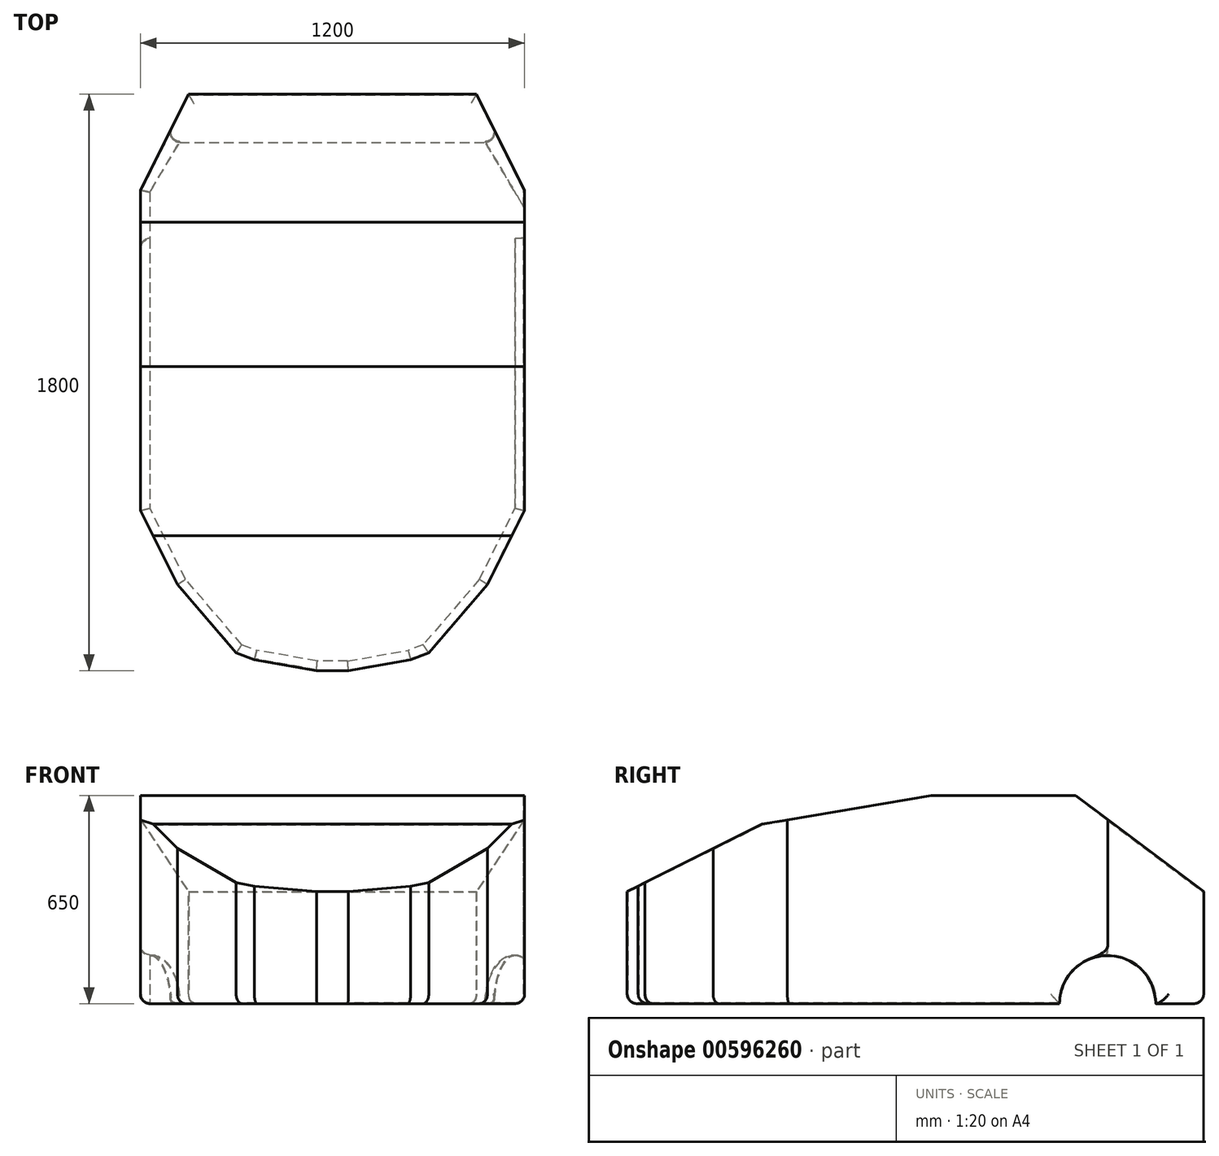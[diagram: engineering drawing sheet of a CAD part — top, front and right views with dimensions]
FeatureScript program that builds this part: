
annotation { "Feature Type Name" : "Feature", "Feature Type Description" : "" }
export const myFeature = defineFeature(function(context is Context, id is Id, definition is map)
    precondition{}
    {
        {
            var Q0;
            Q0=qCreatedBy(makeId("Top.planeOp"),FACE);
            var sketch = newSketch(context, id + "F0", { "sketchPlane" : qUnion([Q0])});
            skLineSegment(sketch, "E0.bottom", {"start": v(600, 900) * mm, "end": v(-600, 900) * mm});
            skLineSegment(sketch, "E0.top", {"start": v(600, -900) * mm, "end": v(-600, -900) * mm});
            skLineSegment(sketch, "E0.left", {"start": v(600, 900) * mm, "end": v(600, -900) * mm});
            skLineSegment(sketch, "E0.right", {"start": v(-600, 900) * mm, "end": v(-600, -900) * mm});
            skPoint(sketch, "E0.middle", {"position": v(0, 0) * mm});
            skSolve(sketch);
        }
        {
            var Q0;
            Q0=makeQuery(id+"F0.imprint","IMPRINT",FACE,{"disambiguationData":[TD([[makeQuery(id+"F0.imprint","IMPRINT",EDGE,{"derivedFrom":sQuery(id+"F0.wireOp",EDGE,"E0.bottom")}),1.0]])]});
            extrude(context, id + "F1", {"entities" : qUnion([Q0]), "depth" : 650 * mm, "offsetDistance" : 25 * mm});
        }
        {
            var Q0;
            Q0=makeQuery(id+"F1.opExtrude","CAP_EDGE",EDGE,{"disambiguationData":[OSD([sQuery(id+"F0.wireOp",EDGE,"E0.top")])],"isStart":false});
            chamfer(context, id + "F2", {"entities" : qUnion([Q0]), "chamferType" : ChamferType.TWO_OFFSETS, "width1" : 300 * mm, "oppositeDirection" : false, "width2" : 600 * mm, "tangentPropagation" : true});
        }
        {
            var Q0;
            Q0=makeQuery(id+"F1.opExtrude","CAP_EDGE",EDGE,{"disambiguationData":[OSD([sQuery(id+"F0.wireOp",EDGE,"E0.bottom")])],"isStart":false});
            chamfer(context, id + "F3", {"entities" : qUnion([Q0]), "chamferType" : ChamferType.TWO_OFFSETS, "width1" : 400 * mm, "oppositeDirection" : false, "width2" : 300 * mm, "tangentPropagation" : true});
        }
        {
            var Q0;
            Q0=makeQuery(id+"F1.opExtrude","SWEPT_EDGE",EDGE,{"disambiguationData":[OSD([sQuery(id+"F0.wireOp",EDGE,"E0.top"),sQuery(id+"F0.wireOp",EDGE,"E0.left")])]});
            var Q1;
            Q1=makeQuery(id+"F1.opExtrude","SWEPT_EDGE",EDGE,{"disambiguationData":[OSD([sQuery(id+"F0.wireOp",EDGE,"E0.top"),sQuery(id+"F0.wireOp",EDGE,"E0.right")])]});
            chamfer(context, id + "F4", {"entities" : qUnion([Q0, Q1]), "chamferType" : ChamferType.TWO_OFFSETS, "width1" : 500 * mm, "oppositeDirection" : false, "width2" : 250 * mm, "tangentPropagation" : true});
        }
        {
            var Q0;
            {var subQ0=sQuery(id+"F0.wireOp",EDGE,"E0.top");Q0=makeQuery(id+"F4.opChamfer","BLEND_EDGE",EDGE,{"blendedFrom":[makeQuery(id+"F1.opExtrude","SWEPT_EDGE",EDGE,{"disambiguationData":[OSD([subQ0,sQuery(id+"F0.wireOp",EDGE,"E0.left")])]}),makeQuery(id+"F1.opExtrude","SWEPT_FACE",FACE,{"disambiguationData":[OSD([subQ0])]})],"blendedInto":[makeQuery(id+"F1.opExtrude","SWEPT_FACE",FACE,{"disambiguationData":[OSD([subQ0])]})]});}
            var Q1;
            {var subQ0=sQuery(id+"F0.wireOp",EDGE,"E0.top");Q1=makeQuery(id+"F4.opChamfer","BLEND_EDGE",EDGE,{"blendedFrom":[makeQuery(id+"F1.opExtrude","SWEPT_EDGE",EDGE,{"disambiguationData":[OSD([subQ0,sQuery(id+"F0.wireOp",EDGE,"E0.right")])]}),makeQuery(id+"F1.opExtrude","SWEPT_FACE",FACE,{"disambiguationData":[OSD([subQ0])]})],"blendedInto":[makeQuery(id+"F1.opExtrude","SWEPT_FACE",FACE,{"disambiguationData":[OSD([subQ0])]})]});}
            chamfer(context, id + "F5", {"entities" : qUnion([Q0, Q1]), "chamferType" : ChamferType.TWO_OFFSETS, "width1" : 200 * mm, "oppositeDirection" : false, "width2" : 100 * mm, "tangentPropagation" : true});
        }
        {
            var Q0;
            {var subQ0=sQuery(id+"F0.wireOp",EDGE,"E0.top");var subQ1=makeQuery(id+"F1.opExtrude","SWEPT_FACE",FACE,{"disambiguationData":[OSD([subQ0])]});Q0=makeQuery(id+"F5.opChamfer","BLEND_EDGE",EDGE,{"blendedFrom":[makeQuery(id+"F4.opChamfer","BLEND_EDGE",EDGE,{"blendedFrom":[makeQuery(id+"F1.opExtrude","SWEPT_EDGE",EDGE,{"disambiguationData":[OSD([subQ0,sQuery(id+"F0.wireOp",EDGE,"E0.right")])]}),subQ1],"blendedInto":[subQ1]}),subQ1],"blendedInto":[subQ1]});}
            var Q1;
            {var subQ0=sQuery(id+"F0.wireOp",EDGE,"E0.top");var subQ1=makeQuery(id+"F1.opExtrude","SWEPT_FACE",FACE,{"disambiguationData":[OSD([subQ0])]});Q1=makeQuery(id+"F5.opChamfer","BLEND_EDGE",EDGE,{"blendedFrom":[makeQuery(id+"F4.opChamfer","BLEND_EDGE",EDGE,{"blendedFrom":[makeQuery(id+"F1.opExtrude","SWEPT_EDGE",EDGE,{"disambiguationData":[OSD([subQ0,sQuery(id+"F0.wireOp",EDGE,"E0.left")])]}),subQ1],"blendedInto":[subQ1]}),subQ1],"blendedInto":[subQ1]});}
            chamfer(context, id + "F6", {"entities" : qUnion([Q0, Q1]), "chamferType" : ChamferType.TWO_OFFSETS, "width1" : 100 * mm, "oppositeDirection" : false, "width2" : 100 * mm, "tangentPropagation" : true});
        }
        {
            var Q0;
            {var subQ0=sQuery(id+"F0.wireOp",EDGE,"E0.top");Q0=makeQuery(id+"F2.opChamfer","BLEND_EDGE",EDGE,{"blendedFrom":[makeQuery(id+"F1.opExtrude","CAP_EDGE",EDGE,{"disambiguationData":[OSD([subQ0])],"isStart":false}),makeQuery(id+"F1.opExtrude","CAP_FACE",FACE,{"disambiguationData":[OSD([sQuery(id+"F0.wireOp",EDGE,"E0.bottom"),subQ0,sQuery(id+"F0.wireOp",EDGE,"E0.left"),sQuery(id+"F0.wireOp",EDGE,"E0.right")])],"isStart":false})],"blendedInto":[makeQuery(id+"F1.opExtrude","CAP_FACE",FACE,{"disambiguationData":[OSD([sQuery(id+"F0.wireOp",EDGE,"E0.bottom"),subQ0,sQuery(id+"F0.wireOp",EDGE,"E0.left"),sQuery(id+"F0.wireOp",EDGE,"E0.right")])],"isStart":false})]});}
            chamfer(context, id + "F7", {"entities" : qUnion([Q0]), "chamferType" : ChamferType.TWO_OFFSETS, "width1" : 350 * mm, "oppositeDirection" : false, "width2" : 200 * mm, "tangentPropagation" : true});
        }
        {
            var Q0;
            Q0=makeQuery(id+"F1.opExtrude","SWEPT_EDGE",EDGE,{"disambiguationData":[OSD([sQuery(id+"F0.wireOp",EDGE,"E0.bottom"),sQuery(id+"F0.wireOp",EDGE,"E0.left")])]});
            var Q1;
            Q1=makeQuery(id+"F1.opExtrude","SWEPT_EDGE",EDGE,{"disambiguationData":[OSD([sQuery(id+"F0.wireOp",EDGE,"E0.bottom"),sQuery(id+"F0.wireOp",EDGE,"E0.right")])]});
            chamfer(context, id + "F8", {"entities" : qUnion([Q0, Q1]), "chamferType" : ChamferType.TWO_OFFSETS, "width1" : 150 * mm, "oppositeDirection" : false, "width2" : 300 * mm, "tangentPropagation" : true});
        }
        {
            var Q0;
            {var subQ0=sQuery(id+"F0.wireOp",EDGE,"E0.left");var subQ1=sQuery(id+"F0.wireOp",EDGE,"E0.top");Q0=makeQuery(id+"F5.opChamfer","BLEND_EDGE",EDGE,{"blendedFrom":[makeQuery(id+"F4.opChamfer","BLEND_EDGE",EDGE,{"blendedFrom":[makeQuery(id+"F1.opExtrude","SWEPT_EDGE",EDGE,{"disambiguationData":[OSD([subQ1,subQ0])]}),makeQuery(id+"F1.opExtrude","SWEPT_FACE",FACE,{"disambiguationData":[OSD([subQ1])]})],"blendedInto":[makeQuery(id+"F1.opExtrude","SWEPT_FACE",FACE,{"disambiguationData":[OSD([subQ1])]})]}),makeQuery(id+"F4.opChamfer","BLEND_FACE",FACE,{"disambiguationData":[OSD([subQ1,subQ0])]})],"blendedInto":[makeQuery(id+"F4.opChamfer","BLEND_FACE",FACE,{"disambiguationData":[OSD([subQ1,subQ0])]})]});}
            var Q1;
            {var subQ0=sQuery(id+"F0.wireOp",EDGE,"E0.right");var subQ1=sQuery(id+"F0.wireOp",EDGE,"E0.top");Q1=makeQuery(id+"F5.opChamfer","BLEND_EDGE",EDGE,{"blendedFrom":[makeQuery(id+"F4.opChamfer","BLEND_EDGE",EDGE,{"blendedFrom":[makeQuery(id+"F1.opExtrude","SWEPT_EDGE",EDGE,{"disambiguationData":[OSD([subQ1,subQ0])]}),makeQuery(id+"F1.opExtrude","SWEPT_FACE",FACE,{"disambiguationData":[OSD([subQ1])]})],"blendedInto":[makeQuery(id+"F1.opExtrude","SWEPT_FACE",FACE,{"disambiguationData":[OSD([subQ1])]})]}),makeQuery(id+"F4.opChamfer","BLEND_FACE",FACE,{"disambiguationData":[OSD([subQ1,subQ0])]})],"blendedInto":[makeQuery(id+"F4.opChamfer","BLEND_FACE",FACE,{"disambiguationData":[OSD([subQ1,subQ0])]})]});}
            chamfer(context, id + "F9", {"entities" : qUnion([Q0, Q1]), "chamferType" : ChamferType.TWO_OFFSETS, "width1" : 200 * mm, "oppositeDirection" : false, "width2" : 100 * mm, "tangentPropagation" : true});
        }
        {
            var Q0;
            Q0=makeQuery(id+"F1.opExtrude","SWEPT_FACE",FACE,{"disambiguationData":[OSD([sQuery(id+"F0.wireOp",EDGE,"E0.left")])]});
            var sketch = newSketch(context, id + "F10", { "sketchPlane" : qUnion([Q0])});
            skLineSegment(sketch, "E1", {"start": v(0, -206.83) * mm, "end": v(0, 221.63) * mm});
            skLineSegment(sketch, "E2", {"start": v(-1009.18, 0) * mm, "end": v(1127.85, 0) * mm});
            skLineSegment(sketch, "E3.0", {"start": v(-600, -206.83) * mm, "end": v(-600, 221.63) * mm});
            skLineSegment(sketch, "E4.0", {"start": v(600, -206.83) * mm, "end": v(600, 221.63) * mm});
            skCircle(sketch, "E5", {"center": v(-600, 0) * mm, "radius": 150 * mm});
            skCircle(sketch, "E6", {"center": v(600, 0) * mm, "radius": 150 * mm});
            skSolve(sketch);
        }
        {
            var Q0;
            {var subQ0=sQuery(id+"F10.wireOp",EDGE,"E5");var subQ1=sQuery(id+"F10.wireOp",EDGE,"E2");var subQ2=makeQuery(id+"F10.imprint","INTERSECT",VERTEX,{"disambiguationData":[OD(0.0)],"derivedFrom":[subQ1,subQ0]});Q0=makeQuery(id+"F10.imprint","IMPRINT",FACE,{"disambiguationData":[TD([[makeQuery(id+"F10.imprint","IMPRINT",EDGE,{"disambiguationData":[TD([[subQ2,-1.0]])],"derivedFrom":subQ1}),-1.0]])]});}
            var Q1;
            {var subQ0=sQuery(id+"F10.wireOp",EDGE,"E5");var subQ1=sQuery(id+"F10.wireOp",EDGE,"E2");var subQ2=makeQuery(id+"F10.imprint","INTERSECT",VERTEX,{"disambiguationData":[OD(1.0)],"derivedFrom":[subQ1,subQ0]});Q1=makeQuery(id+"F10.imprint","IMPRINT",FACE,{"disambiguationData":[TD([[makeQuery(id+"F10.imprint","IMPRINT",EDGE,{"disambiguationData":[TD([[subQ2,1.0]])],"derivedFrom":subQ1}),-1.0]])]});}
            var Q2;
            {var subQ0=sQuery(id+"F10.wireOp",EDGE,"E5");var subQ1=sQuery(id+"F10.wireOp",EDGE,"E2");var subQ2=makeQuery(id+"F10.imprint","INTERSECT",VERTEX,{"disambiguationData":[OD(1.0)],"derivedFrom":[subQ1,subQ0]});Q2=makeQuery(id+"F10.imprint","IMPRINT",FACE,{"disambiguationData":[TD([[makeQuery(id+"F10.imprint","IMPRINT",EDGE,{"disambiguationData":[TD([[subQ2,1.0]])],"derivedFrom":subQ1}),1.0]])]});}
            var Q3;
            {var subQ0=sQuery(id+"F10.wireOp",EDGE,"E5");var subQ1=sQuery(id+"F10.wireOp",EDGE,"E2");var subQ2=makeQuery(id+"F10.imprint","INTERSECT",VERTEX,{"disambiguationData":[OD(0.0)],"derivedFrom":[subQ1,subQ0]});Q3=makeQuery(id+"F10.imprint","IMPRINT",FACE,{"disambiguationData":[TD([[makeQuery(id+"F10.imprint","IMPRINT",EDGE,{"disambiguationData":[TD([[subQ2,-1.0]])],"derivedFrom":subQ1}),1.0]])]});}
            var Q4;
            {var subQ1=sQuery(id+"F10.wireOp",EDGE,"E2");var subQ3=sQuery(id+"F10.wireOp",EDGE,"E6");var subQ4=makeQuery(id+"F10.imprint","INTERSECT",VERTEX,{"disambiguationData":[OD(1.0)],"derivedFrom":[subQ1,subQ3]});Q4=makeQuery(id+"F10.imprint","IMPRINT",FACE,{"disambiguationData":[TD([[makeQuery(id+"F10.imprint","IMPRINT",EDGE,{"disambiguationData":[TD([[subQ4,1.0]])],"derivedFrom":subQ1}),1.0]])]});}
            var Q5;
            {var subQ1=sQuery(id+"F10.wireOp",EDGE,"E2");var subQ3=sQuery(id+"F10.wireOp",EDGE,"E6");var subQ4=makeQuery(id+"F10.imprint","INTERSECT",VERTEX,{"disambiguationData":[OD(0.0)],"derivedFrom":[subQ1,subQ3]});Q5=makeQuery(id+"F10.imprint","IMPRINT",FACE,{"disambiguationData":[TD([[makeQuery(id+"F10.imprint","IMPRINT",EDGE,{"disambiguationData":[TD([[subQ4,1.0]])],"derivedFrom":subQ1}),-1.0]])]});}
            var Q6;
            {var subQ1=sQuery(id+"F10.wireOp",EDGE,"E2");var subQ3=sQuery(id+"F10.wireOp",EDGE,"E6");var subQ4=makeQuery(id+"F10.imprint","INTERSECT",VERTEX,{"disambiguationData":[OD(1.0)],"derivedFrom":[subQ1,subQ3]});Q6=makeQuery(id+"F10.imprint","IMPRINT",FACE,{"disambiguationData":[TD([[makeQuery(id+"F10.imprint","IMPRINT",EDGE,{"disambiguationData":[TD([[subQ4,1.0]])],"derivedFrom":subQ1}),-1.0]])]});}
            var Q7;
            {var subQ1=sQuery(id+"F10.wireOp",EDGE,"E2");var subQ3=sQuery(id+"F10.wireOp",EDGE,"E6");var subQ4=makeQuery(id+"F10.imprint","INTERSECT",VERTEX,{"disambiguationData":[OD(0.0)],"derivedFrom":[subQ1,subQ3]});Q7=makeQuery(id+"F10.imprint","IMPRINT",FACE,{"disambiguationData":[TD([[makeQuery(id+"F10.imprint","IMPRINT",EDGE,{"disambiguationData":[TD([[subQ4,1.0]])],"derivedFrom":subQ1}),1.0]])]});}
            extrude(context, id + "F11", {"entities" : qUnion([Q0, Q1, Q2, Q3, Q4, Q5, Q6, Q7]), "operationType" : NewBodyOperationType.REMOVE, "endBound" : BoundingType.THROUGH_ALL, "oppositeDirection" : true, "depth" : 25 * mm, "offsetDistance" : 25 * mm});
        }
        {
            var Q0;
            {var subQ0=sQuery(id+"F0.wireOp",EDGE,"E0.right");var subQ1=sQuery(id+"F0.wireOp",EDGE,"E0.top");var subQ2=makeQuery(id+"F1.opExtrude","SWEPT_FACE",FACE,{"disambiguationData":[OSD([subQ1])]});Q0=makeQuery(id+"F6.opChamfer","BLEND_EDGE",EDGE,{"blendedFrom":[makeQuery(id+"F5.opChamfer","BLEND_EDGE",EDGE,{"blendedFrom":[makeQuery(id+"F4.opChamfer","BLEND_EDGE",EDGE,{"blendedFrom":[makeQuery(id+"F1.opExtrude","SWEPT_EDGE",EDGE,{"disambiguationData":[OSD([subQ1,subQ0])]}),subQ2],"blendedInto":[subQ2]}),subQ2],"blendedInto":[subQ2]}),makeQuery(id+"F1.opExtrude","CAP_FACE",FACE,{"disambiguationData":[OSD([sQuery(id+"F0.wireOp",EDGE,"E0.bottom"),subQ1,sQuery(id+"F0.wireOp",EDGE,"E0.left"),subQ0])],"isStart":true})],"blendedInto":[makeQuery(id+"F1.opExtrude","CAP_FACE",FACE,{"disambiguationData":[OSD([sQuery(id+"F0.wireOp",EDGE,"E0.bottom"),subQ1,sQuery(id+"F0.wireOp",EDGE,"E0.left"),subQ0])],"isStart":true})]});}
            var Q1;
            {var subQ0=sQuery(id+"F0.wireOp",EDGE,"E0.right");var subQ1=sQuery(id+"F0.wireOp",EDGE,"E0.top");Q1=makeQuery(id+"F5.opChamfer","BLEND_EDGE",EDGE,{"blendedFrom":[makeQuery(id+"F4.opChamfer","BLEND_EDGE",EDGE,{"blendedFrom":[makeQuery(id+"F1.opExtrude","SWEPT_EDGE",EDGE,{"disambiguationData":[OSD([subQ1,subQ0])]}),makeQuery(id+"F1.opExtrude","SWEPT_FACE",FACE,{"disambiguationData":[OSD([subQ1])]})],"blendedInto":[makeQuery(id+"F1.opExtrude","SWEPT_FACE",FACE,{"disambiguationData":[OSD([subQ1])]})]}),makeQuery(id+"F1.opExtrude","CAP_FACE",FACE,{"disambiguationData":[OSD([sQuery(id+"F0.wireOp",EDGE,"E0.bottom"),subQ1,sQuery(id+"F0.wireOp",EDGE,"E0.left"),subQ0])],"isStart":true})],"blendedInto":[makeQuery(id+"F1.opExtrude","CAP_FACE",FACE,{"disambiguationData":[OSD([sQuery(id+"F0.wireOp",EDGE,"E0.bottom"),subQ1,sQuery(id+"F0.wireOp",EDGE,"E0.left"),subQ0])],"isStart":true})]});}
            var Q2;
            {var subQ0=sQuery(id+"F0.wireOp",EDGE,"E0.right");var subQ1=sQuery(id+"F0.wireOp",EDGE,"E0.top");Q2=makeQuery(id+"F9.opChamfer","BLEND_EDGE",EDGE,{"blendedFrom":[makeQuery(id+"F5.opChamfer","BLEND_EDGE",EDGE,{"blendedFrom":[makeQuery(id+"F4.opChamfer","BLEND_EDGE",EDGE,{"blendedFrom":[makeQuery(id+"F1.opExtrude","SWEPT_EDGE",EDGE,{"disambiguationData":[OSD([subQ1,subQ0])]}),makeQuery(id+"F1.opExtrude","SWEPT_FACE",FACE,{"disambiguationData":[OSD([subQ1])]})],"blendedInto":[makeQuery(id+"F1.opExtrude","SWEPT_FACE",FACE,{"disambiguationData":[OSD([subQ1])]})]}),makeQuery(id+"F4.opChamfer","BLEND_FACE",FACE,{"disambiguationData":[OSD([subQ1,subQ0])]})],"blendedInto":[makeQuery(id+"F4.opChamfer","BLEND_FACE",FACE,{"disambiguationData":[OSD([subQ1,subQ0])]})]}),makeQuery(id+"F1.opExtrude","CAP_FACE",FACE,{"disambiguationData":[OSD([sQuery(id+"F0.wireOp",EDGE,"E0.bottom"),subQ1,sQuery(id+"F0.wireOp",EDGE,"E0.left"),subQ0])],"isStart":true})],"blendedInto":[makeQuery(id+"F1.opExtrude","CAP_FACE",FACE,{"disambiguationData":[OSD([sQuery(id+"F0.wireOp",EDGE,"E0.bottom"),subQ1,sQuery(id+"F0.wireOp",EDGE,"E0.left"),subQ0])],"isStart":true})]});}
            var Q3;
            Q3=makeQuery(id+"F1.opExtrude","CAP_EDGE",EDGE,{"disambiguationData":[OSD([sQuery(id+"F0.wireOp",EDGE,"E0.top")])],"isStart":true});
            var Q4;
            {var subQ0=sQuery(id+"F0.wireOp",EDGE,"E0.left");var subQ1=sQuery(id+"F0.wireOp",EDGE,"E0.top");var subQ2=makeQuery(id+"F1.opExtrude","SWEPT_FACE",FACE,{"disambiguationData":[OSD([subQ1])]});Q4=makeQuery(id+"F6.opChamfer","BLEND_EDGE",EDGE,{"blendedFrom":[makeQuery(id+"F5.opChamfer","BLEND_EDGE",EDGE,{"blendedFrom":[makeQuery(id+"F4.opChamfer","BLEND_EDGE",EDGE,{"blendedFrom":[makeQuery(id+"F1.opExtrude","SWEPT_EDGE",EDGE,{"disambiguationData":[OSD([subQ1,subQ0])]}),subQ2],"blendedInto":[subQ2]}),subQ2],"blendedInto":[subQ2]}),makeQuery(id+"F1.opExtrude","CAP_FACE",FACE,{"disambiguationData":[OSD([sQuery(id+"F0.wireOp",EDGE,"E0.bottom"),subQ1,subQ0,sQuery(id+"F0.wireOp",EDGE,"E0.right")])],"isStart":true})],"blendedInto":[makeQuery(id+"F1.opExtrude","CAP_FACE",FACE,{"disambiguationData":[OSD([sQuery(id+"F0.wireOp",EDGE,"E0.bottom"),subQ1,subQ0,sQuery(id+"F0.wireOp",EDGE,"E0.right")])],"isStart":true})]});}
            var Q5;
            {var subQ0=sQuery(id+"F0.wireOp",EDGE,"E0.left");var subQ1=sQuery(id+"F0.wireOp",EDGE,"E0.top");Q5=makeQuery(id+"F5.opChamfer","BLEND_EDGE",EDGE,{"blendedFrom":[makeQuery(id+"F4.opChamfer","BLEND_EDGE",EDGE,{"blendedFrom":[makeQuery(id+"F1.opExtrude","SWEPT_EDGE",EDGE,{"disambiguationData":[OSD([subQ1,subQ0])]}),makeQuery(id+"F1.opExtrude","SWEPT_FACE",FACE,{"disambiguationData":[OSD([subQ1])]})],"blendedInto":[makeQuery(id+"F1.opExtrude","SWEPT_FACE",FACE,{"disambiguationData":[OSD([subQ1])]})]}),makeQuery(id+"F1.opExtrude","CAP_FACE",FACE,{"disambiguationData":[OSD([sQuery(id+"F0.wireOp",EDGE,"E0.bottom"),subQ1,subQ0,sQuery(id+"F0.wireOp",EDGE,"E0.right")])],"isStart":true})],"blendedInto":[makeQuery(id+"F1.opExtrude","CAP_FACE",FACE,{"disambiguationData":[OSD([sQuery(id+"F0.wireOp",EDGE,"E0.bottom"),subQ1,subQ0,sQuery(id+"F0.wireOp",EDGE,"E0.right")])],"isStart":true})]});}
            var Q6;
            {var subQ0=sQuery(id+"F0.wireOp",EDGE,"E0.left");var subQ1=sQuery(id+"F0.wireOp",EDGE,"E0.top");Q6=makeQuery(id+"F9.opChamfer","BLEND_EDGE",EDGE,{"blendedFrom":[makeQuery(id+"F5.opChamfer","BLEND_EDGE",EDGE,{"blendedFrom":[makeQuery(id+"F4.opChamfer","BLEND_EDGE",EDGE,{"blendedFrom":[makeQuery(id+"F1.opExtrude","SWEPT_EDGE",EDGE,{"disambiguationData":[OSD([subQ1,subQ0])]}),makeQuery(id+"F1.opExtrude","SWEPT_FACE",FACE,{"disambiguationData":[OSD([subQ1])]})],"blendedInto":[makeQuery(id+"F1.opExtrude","SWEPT_FACE",FACE,{"disambiguationData":[OSD([subQ1])]})]}),makeQuery(id+"F4.opChamfer","BLEND_FACE",FACE,{"disambiguationData":[OSD([subQ1,subQ0])]})],"blendedInto":[makeQuery(id+"F4.opChamfer","BLEND_FACE",FACE,{"disambiguationData":[OSD([subQ1,subQ0])]})]}),makeQuery(id+"F1.opExtrude","CAP_FACE",FACE,{"disambiguationData":[OSD([sQuery(id+"F0.wireOp",EDGE,"E0.bottom"),subQ1,subQ0,sQuery(id+"F0.wireOp",EDGE,"E0.right")])],"isStart":true})],"blendedInto":[makeQuery(id+"F1.opExtrude","CAP_FACE",FACE,{"disambiguationData":[OSD([sQuery(id+"F0.wireOp",EDGE,"E0.bottom"),subQ1,subQ0,sQuery(id+"F0.wireOp",EDGE,"E0.right")])],"isStart":true})]});}
            var Q7;
            Q7=makeQuery(id+"F11.boolean.opBoolean","INTERSECT",EDGE,{"derivedFrom":[makeQuery(id+"F9.opChamfer","BLEND_FACE",FACE,{"disambiguationData":[OSD([sQuery(id+"F0.wireOp",EDGE,"E0.top"),sQuery(id+"F0.wireOp",EDGE,"E0.left")])]}),makeQuery(id+"F11.opExtrude","SWEPT_FACE",FACE,{"disambiguationData":[OSD([sQuery(id+"F10.wireOp",EDGE,"E5")])]})]});
            var Q8;
            Q8=makeQuery(id+"F11.boolean.opBoolean","INTERSECT",EDGE,{"derivedFrom":[makeQuery(id+"F4.opChamfer","BLEND_FACE",FACE,{"disambiguationData":[OSD([sQuery(id+"F0.wireOp",EDGE,"E0.top"),sQuery(id+"F0.wireOp",EDGE,"E0.left")])]}),makeQuery(id+"F11.opExtrude","SWEPT_FACE",FACE,{"disambiguationData":[OSD([sQuery(id+"F10.wireOp",EDGE,"E5")])]})]});
            var Q9;
            {var subQ0=sQuery(id+"F0.wireOp",EDGE,"E0.left");var subQ1=sQuery(id+"F0.wireOp",EDGE,"E0.top");Q9=makeQuery(id+"F4.opChamfer","BLEND_EDGE",EDGE,{"blendedFrom":[makeQuery(id+"F1.opExtrude","SWEPT_EDGE",EDGE,{"disambiguationData":[OSD([subQ1,subQ0])]}),makeQuery(id+"F1.opExtrude","CAP_FACE",FACE,{"disambiguationData":[OSD([sQuery(id+"F0.wireOp",EDGE,"E0.bottom"),subQ1,subQ0,sQuery(id+"F0.wireOp",EDGE,"E0.right")])],"isStart":true})],"blendedInto":[makeQuery(id+"F1.opExtrude","CAP_FACE",FACE,{"disambiguationData":[OSD([sQuery(id+"F0.wireOp",EDGE,"E0.bottom"),subQ1,subQ0,sQuery(id+"F0.wireOp",EDGE,"E0.right")])],"isStart":true})]});}
            var Q10;
            Q10=makeQuery(id+"F1.opExtrude","CAP_EDGE",EDGE,{"disambiguationData":[OSD([sQuery(id+"F0.wireOp",EDGE,"E0.left")])],"isStart":true});
            var Q11;
            Q11=makeQuery(id+"F11.boolean.opBoolean","INTERSECT",EDGE,{"derivedFrom":[makeQuery(id+"F8.opChamfer","BLEND_FACE",FACE,{"disambiguationData":[OSD([sQuery(id+"F0.wireOp",EDGE,"E0.bottom"),sQuery(id+"F0.wireOp",EDGE,"E0.left")])]}),makeQuery(id+"F11.opExtrude","SWEPT_FACE",FACE,{"disambiguationData":[OSD([sQuery(id+"F10.wireOp",EDGE,"E6")])]})]});
            var Q12;
            Q12=makeQuery(id+"F11.boolean.opBoolean","COPY",EDGE,{"derivedFrom":makeQuery(id+"F11.opExtrude","CAP_EDGE",EDGE,{"disambiguationData":[OSD([sQuery(id+"F10.wireOp",EDGE,"E6")])],"isStart":true})});
            var Q13;
            {var subQ0=sQuery(id+"F0.wireOp",EDGE,"E0.left");var subQ1=sQuery(id+"F0.wireOp",EDGE,"E0.bottom");Q13=makeQuery(id+"F8.opChamfer","BLEND_EDGE",EDGE,{"blendedFrom":[makeQuery(id+"F1.opExtrude","SWEPT_EDGE",EDGE,{"disambiguationData":[OSD([subQ1,subQ0])]}),makeQuery(id+"F1.opExtrude","CAP_FACE",FACE,{"disambiguationData":[OSD([subQ1,sQuery(id+"F0.wireOp",EDGE,"E0.top"),subQ0,sQuery(id+"F0.wireOp",EDGE,"E0.right")])],"isStart":true})],"blendedInto":[makeQuery(id+"F1.opExtrude","CAP_FACE",FACE,{"disambiguationData":[OSD([subQ1,sQuery(id+"F0.wireOp",EDGE,"E0.top"),subQ0,sQuery(id+"F0.wireOp",EDGE,"E0.right")])],"isStart":true})]});}
            var Q14;
            Q14=makeQuery(id+"F1.opExtrude","CAP_EDGE",EDGE,{"disambiguationData":[OSD([sQuery(id+"F0.wireOp",EDGE,"E0.bottom")])],"isStart":true});
            var Q15;
            {var subQ0=sQuery(id+"F0.wireOp",EDGE,"E0.right");var subQ1=sQuery(id+"F0.wireOp",EDGE,"E0.bottom");Q15=makeQuery(id+"F8.opChamfer","BLEND_EDGE",EDGE,{"blendedFrom":[makeQuery(id+"F1.opExtrude","SWEPT_EDGE",EDGE,{"disambiguationData":[OSD([subQ1,subQ0])]}),makeQuery(id+"F1.opExtrude","CAP_FACE",FACE,{"disambiguationData":[OSD([subQ1,sQuery(id+"F0.wireOp",EDGE,"E0.top"),sQuery(id+"F0.wireOp",EDGE,"E0.left"),subQ0])],"isStart":true})],"blendedInto":[makeQuery(id+"F1.opExtrude","CAP_FACE",FACE,{"disambiguationData":[OSD([subQ1,sQuery(id+"F0.wireOp",EDGE,"E0.top"),sQuery(id+"F0.wireOp",EDGE,"E0.left"),subQ0])],"isStart":true})]});}
            var Q16;
            Q16=makeQuery(id+"F11.boolean.opBoolean","INTERSECT",EDGE,{"derivedFrom":[makeQuery(id+"F8.opChamfer","BLEND_FACE",FACE,{"disambiguationData":[OSD([sQuery(id+"F0.wireOp",EDGE,"E0.bottom"),sQuery(id+"F0.wireOp",EDGE,"E0.right")])]}),makeQuery(id+"F11.opExtrude","SWEPT_FACE",FACE,{"disambiguationData":[OSD([sQuery(id+"F10.wireOp",EDGE,"E6")])]})]});
            var Q17;
            Q17=makeQuery(id+"F11.boolean.opBoolean","INTERSECT",EDGE,{"derivedFrom":[makeQuery(id+"F1.opExtrude","SWEPT_FACE",FACE,{"disambiguationData":[OSD([sQuery(id+"F0.wireOp",EDGE,"E0.right")])]}),makeQuery(id+"F11.opExtrude","SWEPT_FACE",FACE,{"disambiguationData":[OSD([sQuery(id+"F10.wireOp",EDGE,"E6")])]})]});
            var Q18;
            Q18=makeQuery(id+"F1.opExtrude","CAP_EDGE",EDGE,{"disambiguationData":[OSD([sQuery(id+"F0.wireOp",EDGE,"E0.right")])],"isStart":true});
            var Q19;
            Q19=makeQuery(id+"F11.boolean.opBoolean","INTERSECT",EDGE,{"derivedFrom":[makeQuery(id+"F9.opChamfer","BLEND_FACE",FACE,{"disambiguationData":[OSD([sQuery(id+"F0.wireOp",EDGE,"E0.top"),sQuery(id+"F0.wireOp",EDGE,"E0.right")])]}),makeQuery(id+"F11.opExtrude","SWEPT_FACE",FACE,{"disambiguationData":[OSD([sQuery(id+"F10.wireOp",EDGE,"E5")])]})]});
            var Q20;
            Q20=makeQuery(id+"F11.boolean.opBoolean","INTERSECT",EDGE,{"derivedFrom":[makeQuery(id+"F4.opChamfer","BLEND_FACE",FACE,{"disambiguationData":[OSD([sQuery(id+"F0.wireOp",EDGE,"E0.top"),sQuery(id+"F0.wireOp",EDGE,"E0.right")])]}),makeQuery(id+"F11.opExtrude","SWEPT_FACE",FACE,{"disambiguationData":[OSD([sQuery(id+"F10.wireOp",EDGE,"E5")])]})]});
            var Q21;
            {var subQ0=sQuery(id+"F0.wireOp",EDGE,"E0.right");var subQ1=sQuery(id+"F0.wireOp",EDGE,"E0.top");Q21=makeQuery(id+"F4.opChamfer","BLEND_EDGE",EDGE,{"blendedFrom":[makeQuery(id+"F1.opExtrude","SWEPT_EDGE",EDGE,{"disambiguationData":[OSD([subQ1,subQ0])]}),makeQuery(id+"F1.opExtrude","CAP_FACE",FACE,{"disambiguationData":[OSD([sQuery(id+"F0.wireOp",EDGE,"E0.bottom"),subQ1,sQuery(id+"F0.wireOp",EDGE,"E0.left"),subQ0])],"isStart":true})],"blendedInto":[makeQuery(id+"F1.opExtrude","CAP_FACE",FACE,{"disambiguationData":[OSD([sQuery(id+"F0.wireOp",EDGE,"E0.bottom"),subQ1,sQuery(id+"F0.wireOp",EDGE,"E0.left"),subQ0])],"isStart":true})]});}
            fillet(context, id + "F12", {"entities" : qUnion([Q0, Q1, Q2, Q3, Q4, Q5, Q6, Q7, Q8, Q9, Q10, Q11, Q12, Q13, Q14, Q15, Q16, Q17, Q18, Q19, Q20, Q21]), "radius" : 30 * mm, "tangentPropagation" : true, "allowEdgeOverflow" : false});
        }
        {
            var Q0;
            Q0=makeQuery(id+"F11.boolean.opBoolean","COPY",FACE,{"derivedFrom":makeQuery(id+"F11.opExtrude","SWEPT_FACE",FACE,{"disambiguationData":[OSD([sQuery(id+"F10.wireOp",EDGE,"E6")])]})});
            var Q1;
            Q1=makeQuery(id+"F11.boolean.opBoolean","COPY",FACE,{"derivedFrom":makeQuery(id+"F11.opExtrude","SWEPT_FACE",FACE,{"disambiguationData":[OSD([sQuery(id+"F10.wireOp",EDGE,"E5")])]})});
            var Q2;
            {var subQ0=sQuery(id+"F0.wireOp",EDGE,"E0.left");var subQ1=sQuery(id+"F0.wireOp",EDGE,"E0.top");var subQ2=sQuery(id+"F0.wireOp",EDGE,"E0.right");Q2=makeQuery(id+"F11.boolean.opBoolean","SPLIT",FACE,{"disambiguationData":[TD([makeQuery(id+"F1.opExtrude","SWEPT_FACE",FACE,{"disambiguationData":[OSD([subQ0])]})])],"derivedFrom":makeQuery(id+"F1.opExtrude","CAP_FACE",FACE,{"disambiguationData":[OSD([sQuery(id+"F0.wireOp",EDGE,"E0.bottom"),subQ1,subQ0,subQ2])],"isStart":true})});}
            shell(context, id + "F13", {"entities" : qUnion([Q0, Q1, Q2]), "thickness" : 2.5 * mm});
        }
    });
